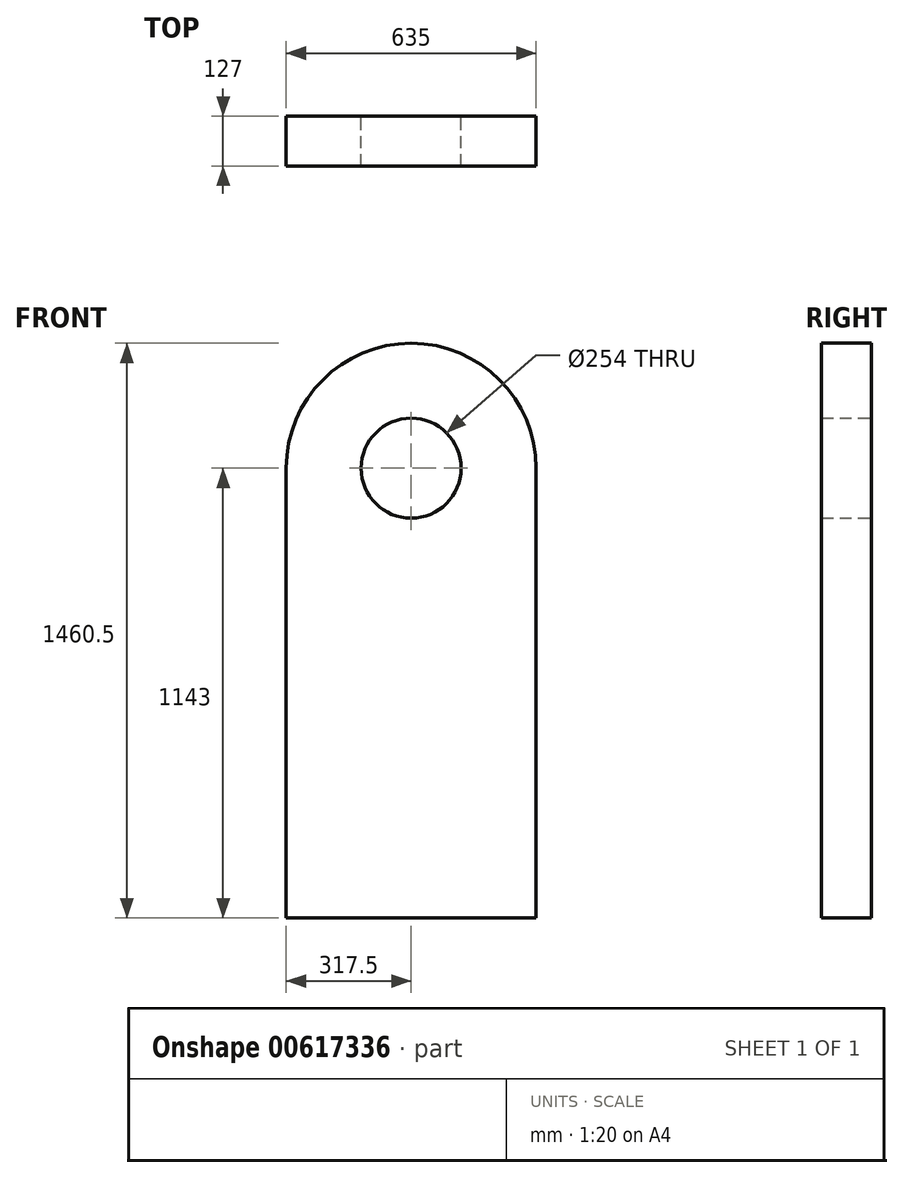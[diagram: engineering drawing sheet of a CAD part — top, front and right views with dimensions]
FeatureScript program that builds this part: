
annotation { "Feature Type Name" : "Feature", "Feature Type Description" : "" }
export const myFeature = defineFeature(function(context is Context, id is Id, definition is map)
    precondition{}
    {
        {
            var Q0;
            Q0=qCreatedBy(makeId("Front.planeOp"),FACE);
            var sketch = newSketch(context, id + "F0", { "sketchPlane" : qUnion([Q0])});
            skCircle(sketch, "E0", {"center": v(0, 641.23) * mm, "radius": 127 * mm});
            skCircle(sketch, "E1", {"center": v(0, 641.23) * mm, "radius": 317.5 * mm});
            skLineSegment(sketch, "E2", {"start": v(-317.5, 641.23) * mm, "end": v(-317.5, -501.77) * mm});
            skLineSegment(sketch, "E3", {"start": v(-317.5, -501.77) * mm, "end": v(317.5, -501.77) * mm});
            skLineSegment(sketch, "E4", {"start": v(317.5, -501.77) * mm, "end": v(317.5, 641.23) * mm});
            skSolve(sketch);
        }
        {
            var Q0;
            Q0 = qSketchRegion(id + "F0", true);
            extrude(context, id + "F1", {"entities" : qUnion([Q0]), "depth" : 127 * mm, "offsetDistance" : 25.4 * mm});
        }
    });
